# Revit family: HM-14_RFA
name_source: partatom
category: Aparatos sanitarios
units: mm (PartAtom-declared; Revit-internal decimal feet)

## family parameters
Compartido = No
Corte con vacíos al cargar = No
Cota de conector redondo = Diámetro de uso
Número OmniClass = 23.45.00.00
Punto de cálculo de habitación = No
Se basa en plano de trabajo = No
Siempre vertical = Sí
Tipo de pieza = Normal
Título OmniClass = Sanitary, Laundry, and Cleaning Equipment

## types (1)
- HM-14
    Brass Chromed = Brass
    Comentarios de tipo = Lavatory Faucet Assemblies
    Descripción = Mezcladora de lavabo 4" sin contra de rejilla
    Elevación por defecto = 0"
    Fabricante = HELVEX
    Features = Valvex II Izq. a 1/4 de vuelta de disco cerámicos
    Imagen de tipo = HM-14.jpg
    Inlet Threads = ½" - 14 NPSM
    Max. Working Pressure = 85.3 psi
    Min. Working Pressure = 3.5 psi
    Modelo = HM-14
    Total Height = 9"
    Total Length = 5"
    Total Width = 6"

## geometry (parser evidence)
native form markers: Sweep x3
no freeform markers — native parametric forms only
